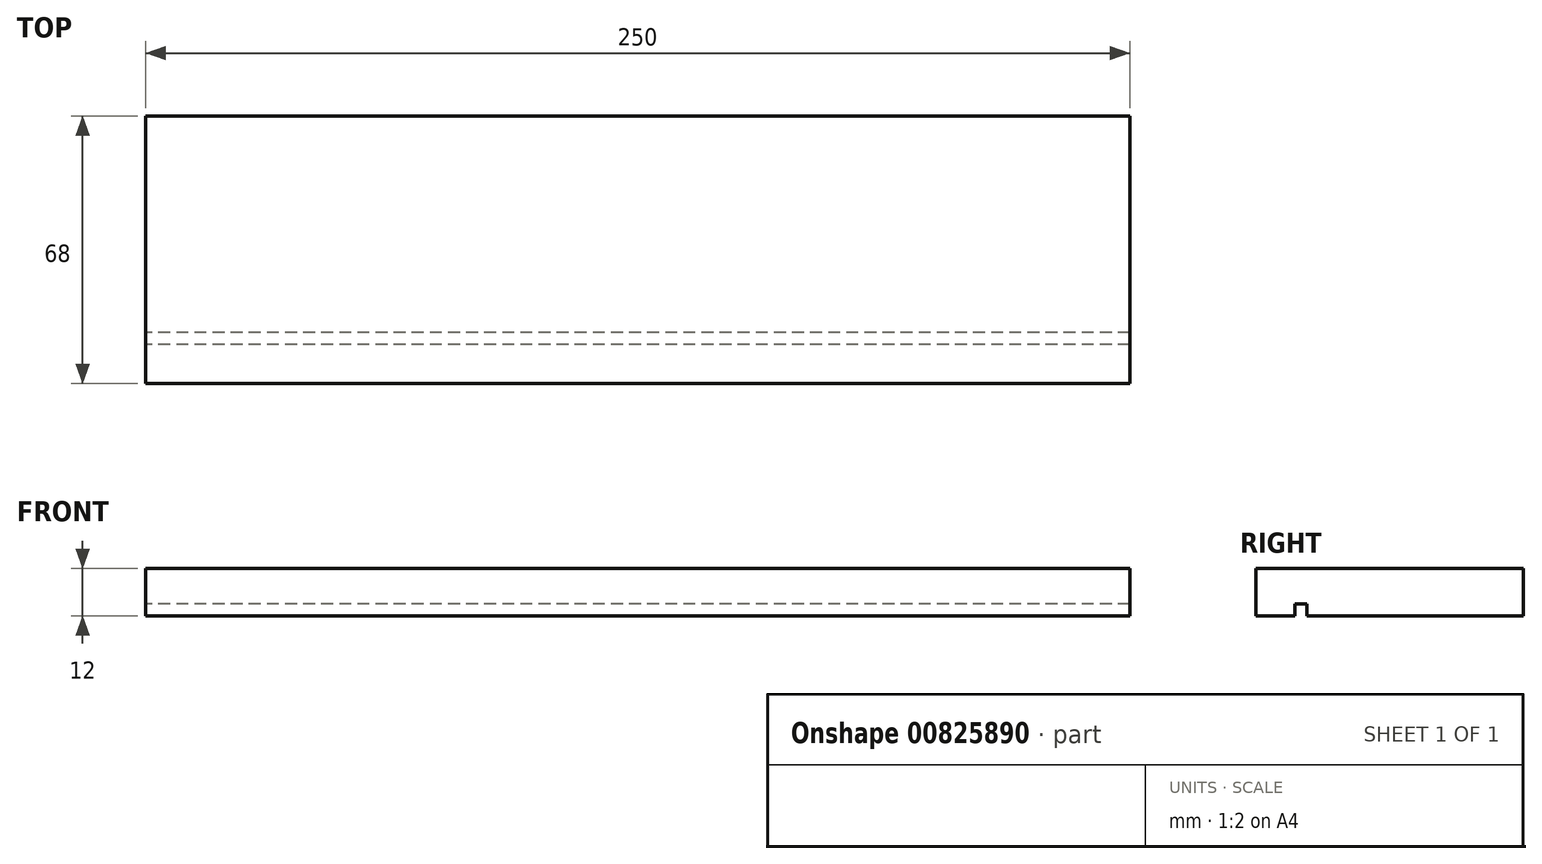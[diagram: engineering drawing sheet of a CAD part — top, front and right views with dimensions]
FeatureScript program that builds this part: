
annotation { "Feature Type Name" : "Feature", "Feature Type Description" : "" }
export const myFeature = defineFeature(function(context is Context, id is Id, definition is map)
    precondition{}
    {
        {
            var Q0;
            Q0=qCreatedBy(makeId("Right.planeOp"),FACE);
            var sketch = newSketch(context, id + "F0", { "sketchPlane" : qUnion([Q0])});
            skLineSegment(sketch, "E0.bottom", {"start": v(34, -6) * mm, "end": v(-34, -6) * mm});
            skLineSegment(sketch, "E0.top", {"start": v(34, 6) * mm, "end": v(-34, 6) * mm});
            skLineSegment(sketch, "E0.left", {"start": v(34, -6) * mm, "end": v(34, 6) * mm});
            skLineSegment(sketch, "E0.right", {"start": v(-34, -6) * mm, "end": v(-34, 6) * mm});
            skPoint(sketch, "E0.middle", {"position": v(0, 0) * mm});
            skLineSegment(sketch, "E1", {"start": v(-24, -6) * mm, "end": v(-24, -3) * mm});
            skLineSegment(sketch, "E2", {"start": v(-24, -3) * mm, "end": v(-21, -3) * mm});
            skLineSegment(sketch, "E3", {"start": v(-21, -3) * mm, "end": v(-21, -6) * mm});
            skSolve(sketch);
        }
        {
            var Q0;
            Q0=makeQuery(id+"F0.imprint","IMPRINT",FACE,{"disambiguationData":[TD([[makeQuery(id+"F0.imprint","IMPRINT",EDGE,{"derivedFrom":sQuery(id+"F0.wireOp",EDGE,"E0.top")}),1.0]])]});
            extrude(context, id + "F1", {"entities" : qUnion([Q0]), "endBound" : BoundingType.SYMMETRIC, "depth" : 250 * mm, "offsetDistance" : 25.4 * mm});
        }
    });
